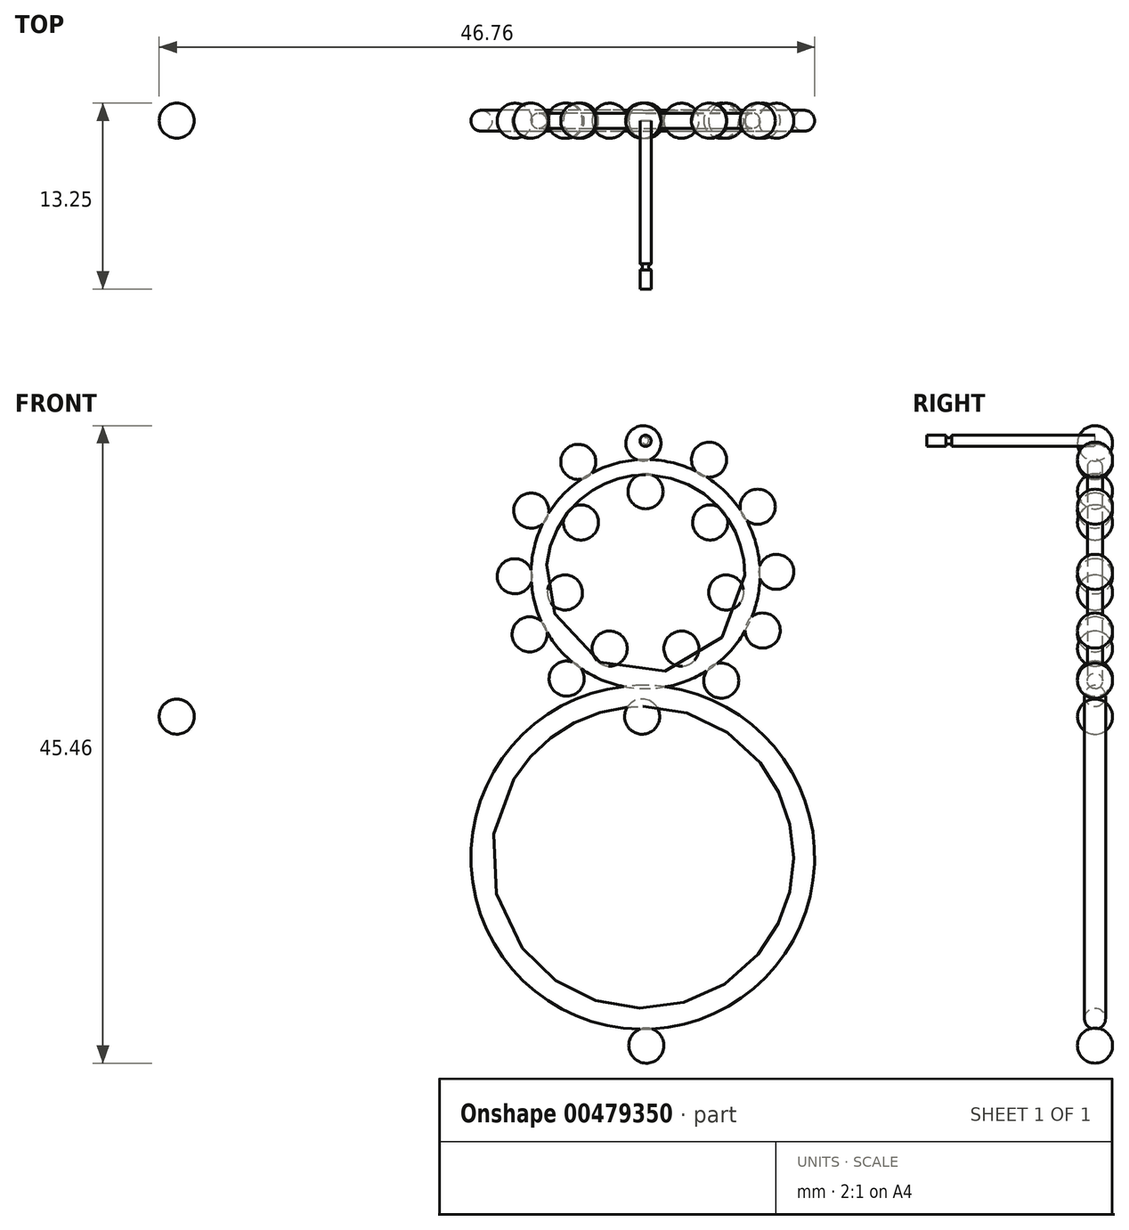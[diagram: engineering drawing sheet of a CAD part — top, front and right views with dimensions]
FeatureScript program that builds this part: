
annotation { "Feature Type Name" : "Feature", "Feature Type Description" : "" }
export const myFeature = defineFeature(function(context is Context, id is Id, definition is map)
    precondition{}
    {
        {
            var Q0;
            Q0=qCreatedBy(makeId("Front.planeOp"),FACE);
            var sketch = newSketch(context, id + "F0", { "sketchPlane" : qUnion([Q0])});
            skCircle(sketch, "E0", {"center": v(0, 0) * mm, "radius": 7 * mm});
            skSolve(sketch);
        }
        {
            var Q0;
            Q0=qCreatedBy(makeId("Top.planeOp"),FACE);
            var sketch = newSketch(context, id + "F1", { "sketchPlane" : qUnion([Q0])});
            skCircle(sketch, "E1", {"center": v(-11.5, 0) * mm, "radius": 0.75 * mm});
            skSolve(sketch);
        }
        {
            var Q0;
            Q0=makeQuery(id+"F1.imprint","IMPRINT",FACE,{"disambiguationData":[TD([[makeQuery(id+"F1.imprint","IMPRINT",EDGE,{"derivedFrom":sQuery(id+"F1.wireOp",EDGE,"E1")}),1.0]])]});
            var Q1;
            Q1=sQuery(id+"F0.wireOp",EDGE,"E0");
            revolve(context, id + "F2", {"entities" : qUnion([Q0]), "axis" : qUnion([Q1]), "revolveType" : RevolveType.FULL});
        }
        {
            var Q0;
            Q0=makeQuery(id+"F2.opRevolve","SWEPT_BODY",BODY,{"disambiguationData":[OSD([sQuery(id+"F1.wireOp",EDGE,"E1")])]});
            transform(context, id + "F3", {"entities" : qUnion([Q0]), "transformType" : TransformType.TRANSLATION_3D, "dx" : 0 * mm, "dy" : 0 * mm, "dz" : -22.7 * mm, "makeCopy" : false});
        }
        {
            var Q0;
            Q0=qCreatedBy(makeId("Top.planeOp"),FACE);
            var sketch = newSketch(context, id + "F4", { "sketchPlane" : qUnion([Q0])});
            skCircle(sketch, "E2", {"center": v(-7.62, 0) * mm, "radius": 0.55 * mm});
            skSolve(sketch);
        }
        {
            var Q0;
            Q0=makeQuery(id+"F4.imprint","IMPRINT",FACE,{"disambiguationData":[TD([[makeQuery(id+"F4.imprint","IMPRINT",EDGE,{"derivedFrom":sQuery(id+"F4.wireOp",EDGE,"E2")}),1.0]])]});
            var Q1;
            Q1=sQuery(id+"F0.wireOp",EDGE,"E0");
            revolve(context, id + "F5", {"entities" : qUnion([Q0]), "axis" : qUnion([Q1]), "revolveType" : RevolveType.FULL});
        }
        {
            var Q0;
            Q0=qCreatedBy(makeId("Front.planeOp"),FACE);
            var sketch = newSketch(context, id + "F6", { "sketchPlane" : qUnion([Q0])});
            skCircle(sketch, "E3", {"center": v(0, 0) * mm, "radius": 1.25 * mm});
            skLineSegment(sketch, "E4", {"start": v(0, 2.25) * mm, "end": v(0, -2.3) * mm});
            skSolve(sketch);
        }
        {
            var Q0;
            {var subQ0=sQuery(id+"F6.wireOp",EDGE,"E4");var subQ1=sQuery(id+"F6.wireOp",EDGE,"E3");var subQ2=makeQuery(id+"F6.imprint","INTERSECT",VERTEX,{"disambiguationData":[OD(0.0)],"derivedFrom":[subQ1,subQ0]});Q0=makeQuery(id+"F6.imprint","IMPRINT",FACE,{"disambiguationData":[TD([[makeQuery(id+"F6.imprint","IMPRINT",EDGE,{"disambiguationData":[TD([[subQ2,1.0]])],"derivedFrom":subQ1}),1.0]])]});}
            var Q1;
            Q1=sQuery(id+"F6.wireOp",EDGE,"E4");
            revolve(context, id + "F7", {"entities" : qUnion([Q0]), "axis" : qUnion([Q1]), "revolveType" : RevolveType.FULL});
        }
        {
            var Q0;
            Q0=makeQuery(id+"F7.opRevolve","SWEPT_BODY",BODY,{"disambiguationData":[OSD([sQuery(id+"F6.wireOp",EDGE,"E3"),sQuery(id+"F6.wireOp",EDGE,"E4")])]});
            transform(context, id + "F8", {"entities" : qUnion([Q0]), "transformType" : TransformType.TRANSLATION_3D, "dx" : 0 * mm, "dy" : 0 * mm, "dz" : 5.9 * mm, "makeCopy" : false});
        }
        {
            var Q0;
            Q0=makeQuery(id+"F7.opRevolve","SWEPT_BODY",BODY,{"disambiguationData":[OSD([sQuery(id+"F6.wireOp",EDGE,"E3"),sQuery(id+"F6.wireOp",EDGE,"E4")])]});
            var Q1;
            Q1=sQuery(id+"F0.wireOp",EDGE,"E0");
            circularPattern(context, id + "F9", {"entities" : qUnion([Q0]), "axis" : qUnion([Q1]), "angle" : 360 * degree, "instanceCount" : 7, "equalSpace" : true});
        }
        {
            var Q0;
            Q0=makeQuery(id+"F7.opRevolve","SWEPT_BODY",BODY,{"disambiguationData":[OSD([sQuery(id+"F6.wireOp",EDGE,"E3"),sQuery(id+"F6.wireOp",EDGE,"E4")])]});
            transform(context, id + "F10", {"entities" : qUnion([Q0]), "transformType" : TransformType.COPY});
        }
        {
            var Q0;
            Q0=makeQuery(id+"F7.opRevolve","SWEPT_BODY",BODY,{"disambiguationData":[OSD([sQuery(id+"F6.wireOp",EDGE,"E3"),sQuery(id+"F6.wireOp",EDGE,"E4")])]});
            transform(context, id + "F11", {"entities" : qUnion([Q0]), "transformType" : TransformType.TRANSLATION_3D, "dx" : -4.8 * mm, "dy" : 0 * mm, "dz" : 2.1 * mm, "makeCopy" : false});
        }
        {
            var Q0;
            Q0=makeQuery(id+"F7.opRevolve","SWEPT_BODY",BODY,{"disambiguationData":[OSD([sQuery(id+"F6.wireOp",EDGE,"E3"),sQuery(id+"F6.wireOp",EDGE,"E4")])]});
            var Q1;
            Q1=sQuery(id+"F0.wireOp",EDGE,"E0");
            circularPattern(context, id + "F12", {"entities" : qUnion([Q0]), "axis" : qUnion([Q1]), "angle" : 360 * degree, "instanceCount" : 12, "equalSpace" : true});
        }
        {
            var Q0;
            Q0=makeQuery(id+"F12.opPattern","COPY",BODY,{"derivedFrom":makeQuery(id+"F7.opRevolve","SWEPT_BODY",BODY,{"disambiguationData":[OSD([sQuery(id+"F6.wireOp",EDGE,"E3"),sQuery(id+"F6.wireOp",EDGE,"E4")])]}),"instanceName":"5"});
            transform(context, id + "F13", {"entities" : qUnion([Q0]), "transformType" : TransformType.TRANSLATION_3D, "dx" : 0.7 * mm, "dy" : 0 * mm, "dz" : -23.5 * mm, "makeCopy" : false});
        }
        {
            var Q0;
            Q0=makeQuery(id+"F12.opPattern","COPY",BODY,{"derivedFrom":makeQuery(id+"F7.opRevolve","SWEPT_BODY",BODY,{"disambiguationData":[OSD([sQuery(id+"F6.wireOp",EDGE,"E3"),sQuery(id+"F6.wireOp",EDGE,"E4")])]}),"instanceName":"6"});
            transform(context, id + "F14", {"entities" : qUnion([Q0]), "transformType" : TransformType.TRANSLATION_3D, "dx" : 1.6 * mm, "dy" : 0 * mm, "dz" : 0.9 * mm, "makeCopy" : false});
        }
        {
            var Q0;
            Q0=makeQuery(id+"F2.opRevolve","SWEPT_BODY",BODY,{"disambiguationData":[OSD([sQuery(id+"F1.wireOp",EDGE,"E1")])]});
            var Q1;
            Q1=makeQuery(id+"F12.opPattern","COPY",BODY,{"derivedFrom":makeQuery(id+"F7.opRevolve","SWEPT_BODY",BODY,{"disambiguationData":[OSD([sQuery(id+"F6.wireOp",EDGE,"E3"),sQuery(id+"F6.wireOp",EDGE,"E4")])]}),"instanceName":"5"});
            transform(context, id + "F15", {"entities" : qUnion([Q0, Q1]), "transformType" : TransformType.TRANSLATION_3D, "dx" : -0.2 * mm, "dy" : 0 * mm, "dz" : 2.5 * mm, "makeCopy" : false});
        }
        {
            var Q0;
            Q0=makeQuery(id+"F12.opPattern","COPY",BODY,{"derivedFrom":makeQuery(id+"F7.opRevolve","SWEPT_BODY",BODY,{"disambiguationData":[OSD([sQuery(id+"F6.wireOp",EDGE,"E3"),sQuery(id+"F6.wireOp",EDGE,"E4")])]}),"instanceName":"5"});
            transform(context, id + "F16", {"entities" : qUnion([Q0]), "transformType" : TransformType.COPY});
        }
        {
            var Q0;
            Q0=makeQuery(id+"F12.opPattern","COPY",BODY,{"derivedFrom":makeQuery(id+"F7.opRevolve","SWEPT_BODY",BODY,{"disambiguationData":[OSD([sQuery(id+"F6.wireOp",EDGE,"E3"),sQuery(id+"F6.wireOp",EDGE,"E4")])]}),"instanceName":"5"});
            transform(context, id + "F17", {"entities" : qUnion([Q0]), "transformType" : TransformType.TRANSLATION_3D, "dx" : -0.9 * mm, "dy" : 0 * mm, "dz" : 20.16 * mm, "makeCopy" : false});
        }
        {
            var Q0;
            Q0=qCreatedBy(makeId("Front.planeOp"),FACE);
            var sketch = newSketch(context, id + "F18", { "sketchPlane" : qUnion([Q0])});
            skCircle(sketch, "E5", {"center": v(0, 0) * mm, "radius": 0.4 * mm});
            skSolve(sketch);
        }
        {
            var Q0;
            Q0=makeQuery(id+"F18.imprint","IMPRINT",FACE,{"disambiguationData":[TD([[makeQuery(id+"F18.imprint","IMPRINT",EDGE,{"derivedFrom":sQuery(id+"F18.wireOp",EDGE,"E5")}),1.0]])]});
            extrude(context, id + "F19", {"entities" : qUnion([Q0]), "depth" : 12 * mm});
        }
        {
            var Q0;
            Q0=makeQuery(id+"F12.opPattern","COPY",BODY,{"derivedFrom":makeQuery(id+"F7.opRevolve","SWEPT_BODY",BODY,{"disambiguationData":[OSD([sQuery(id+"F6.wireOp",EDGE,"E3"),sQuery(id+"F6.wireOp",EDGE,"E4")])]}),"instanceName":"4"});
            transform(context, id + "F20", {"entities" : qUnion([Q0]), "transformType" : TransformType.TRANSLATION_3D, "dx" : -1.1 * mm, "dy" : 0 * mm, "dz" : 0.7 * mm, "makeCopy" : false});
        }
        {
            var Q0;
            Q0=makeQuery(id+"F12.opPattern","COPY",BODY,{"derivedFrom":makeQuery(id+"F7.opRevolve","SWEPT_BODY",BODY,{"disambiguationData":[OSD([sQuery(id+"F6.wireOp",EDGE,"E3"),sQuery(id+"F6.wireOp",EDGE,"E4")])]}),"instanceName":"7"});
            transform(context, id + "F21", {"entities" : qUnion([Q0]), "transformType" : TransformType.TRANSLATION_3D, "dx" : 0.2 * mm, "dy" : 0 * mm, "dz" : 0.5 * mm, "makeCopy" : false});
        }
        {
            var Q0;
            Q0=makeQuery(id+"F12.opPattern","COPY",BODY,{"derivedFrom":makeQuery(id+"F7.opRevolve","SWEPT_BODY",BODY,{"disambiguationData":[OSD([sQuery(id+"F6.wireOp",EDGE,"E3"),sQuery(id+"F6.wireOp",EDGE,"E4")])]}),"instanceName":"3"});
            transform(context, id + "F22", {"entities" : qUnion([Q0]), "transformType" : TransformType.TRANSLATION_3D, "dx" : -0.4 * mm, "dy" : 0 * mm, "dz" : 0.5 * mm, "makeCopy" : false});
        }
        {
            var Q0;
            Q0=makeQuery(id+"F12.opPattern","COPY",BODY,{"derivedFrom":makeQuery(id+"F7.opRevolve","SWEPT_BODY",BODY,{"disambiguationData":[OSD([sQuery(id+"F6.wireOp",EDGE,"E3"),sQuery(id+"F6.wireOp",EDGE,"E4")])]}),"instanceName":"6"});
            transform(context, id + "F23", {"entities" : qUnion([Q0]), "transformType" : TransformType.TRANSLATION_3D, "dx" : -1 * mm, "dy" : 0 * mm, "dz" : -0.5 * mm, "makeCopy" : false});
        }
        {
            var Q0;
            Q0=makeQuery(id+"F12.opPattern","COPY",BODY,{"derivedFrom":makeQuery(id+"F7.opRevolve","SWEPT_BODY",BODY,{"disambiguationData":[OSD([sQuery(id+"F6.wireOp",EDGE,"E3"),sQuery(id+"F6.wireOp",EDGE,"E4")])]}),"instanceName":"3"});
            transform(context, id + "F24", {"entities" : qUnion([Q0]), "transformType" : TransformType.TRANSLATION_3D, "dx" : 0.13 * mm, "dy" : 0 * mm, "dz" : 0 * mm, "makeCopy" : false});
        }
        {
            var Q0;
            Q0=makeQuery(id+"F16.opPattern","COPY",BODY,{"derivedFrom":makeQuery(id+"F12.opPattern","COPY",BODY,{"derivedFrom":makeQuery(id+"F7.opRevolve","SWEPT_BODY",BODY,{"disambiguationData":[OSD([sQuery(id+"F6.wireOp",EDGE,"E3"),sQuery(id+"F6.wireOp",EDGE,"E4")])]}),"instanceName":"5"}),"instanceName":"1"});
            transform(context, id + "F25", {"entities" : qUnion([Q0]), "transformType" : TransformType.TRANSLATION_3D, "dx" : -0.6 * mm, "dy" : 0 * mm, "dz" : -3.3 * mm, "makeCopy" : false});
        }
        {
            var Q0;
            Q0=qCreatedBy(makeId("Top.planeOp"),FACE);
            var sketch = newSketch(context, id + "F26", { "sketchPlane" : qUnion([Q0])});
            skCircle(sketch, "E6", {"center": v(0.43, -10.42) * mm, "radius": 0.21 * mm});
            skSolve(sketch);
        }
        {
            var Q0;
            Q0=makeQuery(id+"F26.imprint","IMPRINT",FACE,{"disambiguationData":[TD([[makeQuery(id+"F26.imprint","IMPRINT",EDGE,{"derivedFrom":sQuery(id+"F26.wireOp",EDGE,"E6")}),1.0]])]});
            var Q1;
            Q1=makeQuery(id+"F19.opExtrude","CAP_EDGE",EDGE,{"disambiguationData":[OSD([sQuery(id+"F18.wireOp",EDGE,"E5")])],"isStart":false});
            revolve(context, id + "F27", {"operationType" : NewBodyOperationType.REMOVE, "entities" : qUnion([Q0]), "axis" : qUnion([Q1]), "revolveType" : RevolveType.FULL, "oppositeDirection" : true});
        }
        {
            var Q0;
            Q0=makeQuery(id+"F19.opExtrude","SWEPT_BODY",BODY,{"disambiguationData":[OSD([sQuery(id+"F18.wireOp",EDGE,"E5")])]});
            transform(context, id + "F28", {"entities" : qUnion([Q0]), "transformType" : TransformType.TRANSLATION_3D, "dx" : 0 * mm, "dy" : 0 * mm, "dz" : 9.5 * mm, "makeCopy" : false});
        }
        {
            var Q0;
            Q0=makeQuery(id+"F12.opPattern","COPY",BODY,{"derivedFrom":makeQuery(id+"F7.opRevolve","SWEPT_BODY",BODY,{"disambiguationData":[OSD([sQuery(id+"F6.wireOp",EDGE,"E3"),sQuery(id+"F6.wireOp",EDGE,"E4")])]}),"instanceName":"5"});
            transform(context, id + "F29", {"entities" : qUnion([Q0]), "transformType" : TransformType.COPY});
        }
        {
            var Q0;
            Q0=makeQuery(id+"F12.opPattern","COPY",BODY,{"derivedFrom":makeQuery(id+"F7.opRevolve","SWEPT_BODY",BODY,{"disambiguationData":[OSD([sQuery(id+"F6.wireOp",EDGE,"E3"),sQuery(id+"F6.wireOp",EDGE,"E4")])]}),"instanceName":"5"});
            transform(context, id + "F30", {"entities" : qUnion([Q0]), "transformType" : TransformType.TRANSLATION_3D, "dx" : -33.2 * mm, "dy" : 0 * mm, "dz" : 0 * mm, "makeCopy" : false});
        }
    });
